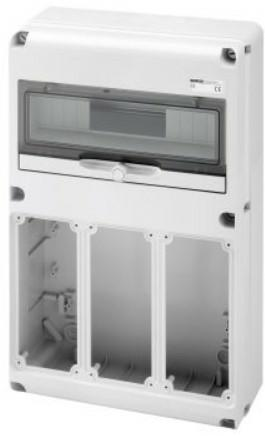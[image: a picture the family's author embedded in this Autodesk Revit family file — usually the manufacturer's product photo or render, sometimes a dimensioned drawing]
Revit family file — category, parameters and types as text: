
# Revit family: Building-QuadriIEC309-GEWISS-68QDIN-QUADRI-PRESE-14MOD_3PRESE_IB_VERT
name_source: partatom
category: Apparecchi elettrici
units: mm (PartAtom-declared; Revit-internal decimal feet)

## family parameters
Condiviso = No
Host = Superficie
Mantenere orientamento annotazione = Sì
Punto di calcolo locali = Sì
Quota connettore circolare = Usa diametro
Taglio con vuoti quando caricato = No
Tipo di parte = Normale

## types (1)
- GW68010N - Q-DIN 14M 3FLANGE PR.BL.VR.SBF IP65
    Catalogo = BUILDING
    Catalogo Serie = 68 QDIN
    Classe isolamento = II
    Codice EAN = 8011564744813
    Codice Electrocod = 2242
    Colore = Grigio RAL 7035
    Conformità normativa = EN 60208 - EN 60670-1 - IEC 60670-24
    Descrizione = Q-DIN 14M 3FLANGE PR.BL.VR.SBF IP65
    Glow Wire Test = 650°C
    Grado di protezione = IP65
    IDF = dc7cd8bb-f800-4397-9026-7208e22c2b9e
    IDT = b7fa234f-6082-4e77-ab12-b88f512de078
    Immagine tipo = GW68010N.jpg
    L_Moduli = 266 mm  [stored 0.872703 ft]
    Modello = GW68010N
    N. IEC 309/IB alloggiabili = 3 IB Vert. 16/32 A IP67
    N. coperchi ciechi in dotazione = 1 IB 16/32 A
    N. flange in dotazione = 1 IB 16/32 A
    N. mod. EN 50022 = 14
    N. prese IB alloggiabili: = 3 IB Vert. 16/32 A IP67
    N. prese alloggiabili = 3 IB Vert. 16/32 A IP67
    N_Moduli = 14 mm  [stored 0.0459318 ft]
    POMELLO = bianco
    PRESA = rosso
    Potenza dissipabile A (W) = 24
    Potenza dissipabile B (W) = 64
    Produttore = GEWISS S.p.A.
    Prospetto di default = 1219 mm
    Resistenza agli urti = IK08
    SEO = Quadretto
    STRUTTURA = RAL - 7035
    STRUTTURA ALTA = Poche
    Scheda Tecnica = https://www.gewiss.com
    Spostamento_S = 1000 mm  [stored 3.28084 ft]
    Temperatura di funzionamento = -25 ÷ +40 °C
    Temperatura di utilizzo = -25 +40 °C
    Termopressione con biglia = 70 °C
    Tipo versione = Vuoto
    Tipologia di installazione = Da parete
    URL = https://www.gewiss.com
    VETRO = Vetro
    Versione file RFA = 21.5

note: [stored X ft] marks values corroborated as IEEE doubles in the binary element streams (Revit-internal decimal feet)

## geometry (parser evidence)
native form markers: Sweep x5
no freeform markers — native parametric forms only
